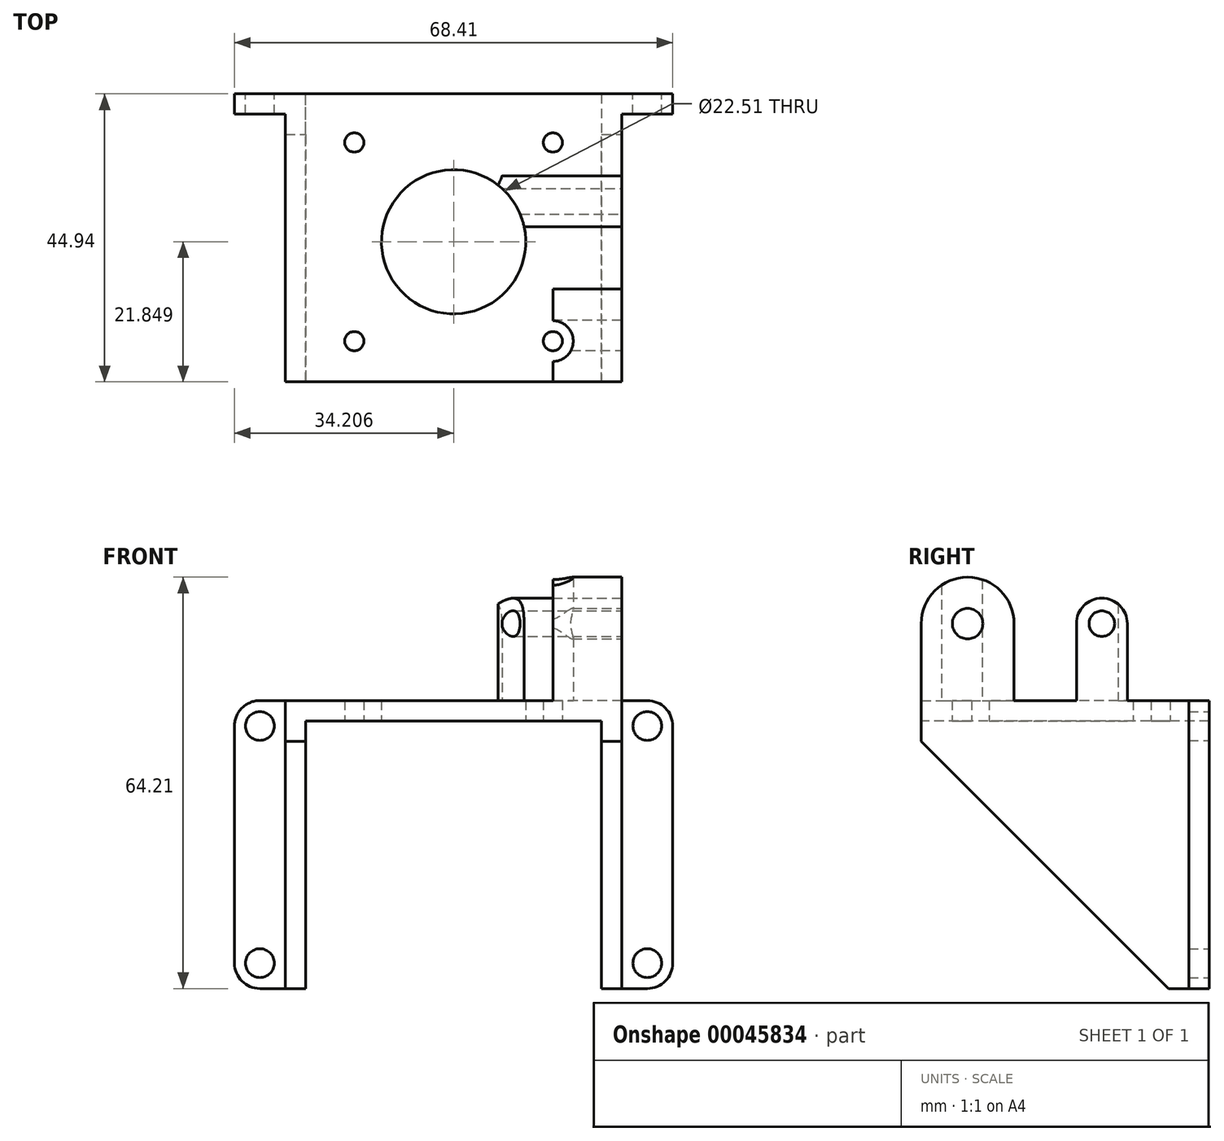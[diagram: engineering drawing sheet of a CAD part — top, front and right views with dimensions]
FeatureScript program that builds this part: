
annotation { "Feature Type Name" : "Feature", "Feature Type Description" : "" }
export const myFeature = defineFeature(function(context is Context, id is Id, definition is map)
    precondition{}
    {
        {
            var Q0;
            Q0=qCreatedBy(makeId("Top.planeOp"),FACE);
            var sketch = newSketch(context, id + "F0", { "sketchPlane" : qUnion([Q0])});
            skLineSegment(sketch, "E0.bottom", {"start": v(0, 0) * mm, "end": v(52.53, 0) * mm});
            skLineSegment(sketch, "E0.top", {"start": v(0, -44.94) * mm, "end": v(52.53, -44.94) * mm});
            skLineSegment(sketch, "E0.left", {"start": v(0, 0) * mm, "end": v(0, -44.94) * mm});
            skLineSegment(sketch, "E0.right", {"start": v(52.53, 0) * mm, "end": v(52.53, -44.94) * mm});
            skLineSegment(sketch, "E1.rect.bottom", {"start": v(41.77, -7.6) * mm, "end": v(10.77, -7.6) * mm, "construction": true});
            skLineSegment(sketch, "E1.rect.top", {"start": v(41.77, -38.6) * mm, "end": v(10.77, -38.6) * mm, "construction": true});
            skLineSegment(sketch, "E1.rect.left", {"start": v(41.77, -7.6) * mm, "end": v(41.77, -38.6) * mm, "construction": true});
            skLineSegment(sketch, "E1.rect.right", {"start": v(10.77, -7.6) * mm, "end": v(10.77, -38.6) * mm, "construction": true});
            skPoint(sketch, "E1.rect.middle", {"position": v(26.27, -23.1) * mm});
            skCircle(sketch, "E2", {"center": v(10.77, -7.6) * mm, "radius": 1.5 * mm});
            skCircle(sketch, "E3", {"center": v(26.27, -23.1) * mm, "radius": 11.25 * mm});
            skCircle(sketch, "E4", {"center": v(41.77, -7.6) * mm, "radius": 1.5 * mm});
            skCircle(sketch, "E5", {"center": v(41.77, -38.6) * mm, "radius": 1.5 * mm});
            skCircle(sketch, "E6", {"center": v(10.77, -38.6) * mm, "radius": 1.5 * mm});
            skLineSegment(sketch, "E7", {"start": v(26.27, -23.1) * mm, "end": v(26.27, 0) * mm, "construction": true});
            skCircle(sketch, "E8", {"center": v(10.77, -38.6) * mm, "radius": 6.35 * mm, "construction": true});
            skSolve(sketch);
        }
        {
            var Q0;
            Q0=qSketchRegion(id+"F0",true);
            extrude(context, id + "F1", {"entities" : qUnion([Q0]), "depth" : 3.17 * mm});
        }
        {
            var Q0;
            Q0=makeQuery(id+"F1.opExtrude","CAP_FACE",FACE,{"disambiguationData":[OSD([sQuery(id+"F0.wireOp",EDGE,"E0.bottom"),sQuery(id+"F0.wireOp",EDGE,"E0.top"),sQuery(id+"F0.wireOp",EDGE,"E0.left"),sQuery(id+"F0.wireOp",EDGE,"E0.right"),sQuery(id+"F0.wireOp",EDGE,"E2"),sQuery(id+"F0.wireOp",EDGE,"E3"),sQuery(id+"F0.wireOp",EDGE,"E4"),sQuery(id+"F0.wireOp",EDGE,"E5"),sQuery(id+"F0.wireOp",EDGE,"E6")])],"isStart":true});
            var sketch = newSketch(context, id + "F2", { "sketchPlane" : qUnion([Q0])});
            skLineSegment(sketch, "E9.bottom", {"start": v(0, 44.94) * mm, "end": v(3.18, 44.94) * mm});
            skLineSegment(sketch, "E9.top", {"start": v(0, 0) * mm, "end": v(3.18, 0) * mm});
            skLineSegment(sketch, "E9.left", {"start": v(0, 44.94) * mm, "end": v(0, 0) * mm});
            skLineSegment(sketch, "E9.right", {"start": v(3.18, 44.94) * mm, "end": v(3.18, 0) * mm});
            skLineSegment(sketch, "E10.bottom", {"start": v(52.53, 0) * mm, "end": v(49.36, 0) * mm});
            skLineSegment(sketch, "E10.top", {"start": v(52.53, 44.94) * mm, "end": v(49.36, 44.94) * mm});
            skLineSegment(sketch, "E10.left", {"start": v(52.53, 0) * mm, "end": v(52.53, 44.94) * mm});
            skLineSegment(sketch, "E10.right", {"start": v(49.36, 0) * mm, "end": v(49.36, 44.94) * mm});
            skSolve(sketch);
        }
        {
            var Q0;
            Q0=qSketchRegion(id+"F2",true);
            extrude(context, id + "F3", {"entities" : qUnion([Q0]), "operationType" : NewBodyOperationType.ADD, "depth" : 41.77 * mm});
        }
        {
            var Q0;
            Q0=makeQuery(id+"F3.opExtrude","CAP_FACE",FACE,{"disambiguationData":[OSD([sQuery(id+"F2.wireOp",EDGE,"E9.bottom"),sQuery(id+"F2.wireOp",EDGE,"E9.top"),sQuery(id+"F2.wireOp",EDGE,"E9.left"),sQuery(id+"F2.wireOp",EDGE,"E9.right")])],"isStart":false});
            var sketch = newSketch(context, id + "F4", { "sketchPlane" : qUnion([Q0])});
            skLineSegment(sketch, "E11.bottom", {"start": v(0, 0) * mm, "end": v(-7.94, 0) * mm});
            skLineSegment(sketch, "E11.top", {"start": v(0, 3.18) * mm, "end": v(-7.94, 3.18) * mm});
            skLineSegment(sketch, "E11.left", {"start": v(0, 0) * mm, "end": v(0, 3.18) * mm});
            skLineSegment(sketch, "E11.right", {"start": v(-7.94, 0) * mm, "end": v(-7.94, 3.18) * mm});
            skLineSegment(sketch, "E12.bottom", {"start": v(52.53, 0) * mm, "end": v(60.47, 0) * mm});
            skLineSegment(sketch, "E12.top", {"start": v(52.53, 3.18) * mm, "end": v(60.47, 3.18) * mm});
            skLineSegment(sketch, "E12.left", {"start": v(52.53, 0) * mm, "end": v(52.53, 3.18) * mm});
            skLineSegment(sketch, "E12.right", {"start": v(60.47, 0) * mm, "end": v(60.47, 3.18) * mm});
            skSolve(sketch);
        }
        {
            var Q0;
            Q0=qSketchRegion(id+"F4",true);
            var Q1;
            Q1=makeQuery(id+"F1.opExtrude","CAP_FACE",FACE,{"disambiguationData":[OSD([sQuery(id+"F0.wireOp",EDGE,"E0.bottom"),sQuery(id+"F0.wireOp",EDGE,"E0.top"),sQuery(id+"F0.wireOp",EDGE,"E0.left"),sQuery(id+"F0.wireOp",EDGE,"E0.right"),sQuery(id+"F0.wireOp",EDGE,"E2"),sQuery(id+"F0.wireOp",EDGE,"E3"),sQuery(id+"F0.wireOp",EDGE,"E4"),sQuery(id+"F0.wireOp",EDGE,"E5"),sQuery(id+"F0.wireOp",EDGE,"E6")])],"isStart":false});
            extrude(context, id + "F5", {"entities" : qUnion([Q0]), "operationType" : NewBodyOperationType.ADD, "endBound" : BoundingType.UP_TO_SURFACE, "oppositeDirection" : true, "endBoundEntityFace" : qUnion([Q1]), "depth" : 25.4 * mm});
        }
        {
            var Q0;
            Q0=makeQuery(id+"F5.opExtrude","CAP_EDGE",EDGE,{"disambiguationData":[OSD([sQuery(id+"F4.wireOp",EDGE,"E12.right")])],"isStart":true});
            var Q1;
            Q1=makeQuery(id+"F5.opExtrude","CAP_EDGE",EDGE,{"disambiguationData":[OSD([sQuery(id+"F4.wireOp",EDGE,"E12.right")])],"isStart":false});
            var Q2;
            Q2=makeQuery(id+"F5.opExtrude","CAP_EDGE",EDGE,{"disambiguationData":[OSD([sQuery(id+"F4.wireOp",EDGE,"E11.right")])],"isStart":false});
            var Q3;
            Q3=makeQuery(id+"F5.opExtrude","CAP_EDGE",EDGE,{"disambiguationData":[OSD([sQuery(id+"F4.wireOp",EDGE,"E11.right")])],"isStart":true});
            fillet(context, id + "F6", {"entities" : qUnion([Q0, Q1, Q2, Q3]), "radius" : 3.97 * mm, "tangentPropagation" : true, "allowEdgeOverflow" : false});
        }
        {
            var Q0;
            Q0=makeQuery(id+"F5.boolean.opBoolean","MERGE",FACE,{"derivedFrom":[makeQuery(id+"F3.boolean.opBoolean","MERGE",FACE,{"derivedFrom":[makeQuery(id+"F1.opExtrude","SWEPT_FACE",FACE,{"disambiguationData":[OSD([sQuery(id+"F0.wireOp",EDGE,"E0.bottom")])]}),makeQuery(id+"F3.opExtrude","SWEPT_FACE",FACE,{"disambiguationData":[OSD([sQuery(id+"F2.wireOp",EDGE,"E9.top")])]}),makeQuery(id+"F3.opExtrude","SWEPT_FACE",FACE,{"disambiguationData":[OSD([sQuery(id+"F2.wireOp",EDGE,"E10.bottom")])]})]}),makeQuery(id+"F5.opExtrude","SWEPT_FACE",FACE,{"disambiguationData":[OSD([sQuery(id+"F4.wireOp",EDGE,"E11.bottom")])]}),makeQuery(id+"F5.opExtrude","SWEPT_FACE",FACE,{"disambiguationData":[OSD([sQuery(id+"F4.wireOp",EDGE,"E12.bottom")])]})]});
            var sketch = newSketch(context, id + "F7", { "sketchPlane" : qUnion([Q0])});
            skCircle(sketch, "E13", {"center": v(3.97, -37.8) * mm, "radius": 2.25 * mm});
            skCircle(sketch, "E14", {"center": v(3.97, -0.8) * mm, "radius": 2.25 * mm});
            skCircle(sketch, "E15", {"center": v(-56.5, -0.8) * mm, "radius": 2.25 * mm});
            skCircle(sketch, "E16", {"center": v(-56.5, -37.8) * mm, "radius": 2.25 * mm});
            skSolve(sketch);
        }
        {
            var Q0;
            Q0=qSketchRegion(id+"F7",true);
            var Q1;
            Q1=makeQuery(id+"F5.opExtrude","SWEPT_FACE",FACE,{"disambiguationData":[OSD([sQuery(id+"F4.wireOp",EDGE,"E12.top")])]});
            extrude(context, id + "F8", {"entities" : qUnion([Q0]), "operationType" : NewBodyOperationType.REMOVE, "endBound" : BoundingType.UP_TO_SURFACE, "oppositeDirection" : true, "endBoundEntityFace" : qUnion([Q1]), "depth" : 25.4 * mm});
        }
        {
            var Q0;
            Q0=makeQuery(id+"F3.boolean.opBoolean","MERGE",FACE,{"derivedFrom":[makeQuery(id+"F1.opExtrude","SWEPT_FACE",FACE,{"disambiguationData":[OSD([sQuery(id+"F0.wireOp",EDGE,"E0.right")])]}),makeQuery(id+"F3.opExtrude","SWEPT_FACE",FACE,{"disambiguationData":[OSD([sQuery(id+"F2.wireOp",EDGE,"E10.left")])]})]});
            var sketch = newSketch(context, id + "F9", { "sketchPlane" : qUnion([Q0])});
            skLineSegment(sketch, "E17.top", {"start": v(-44.94, -41.77) * mm, "end": v(-6.35, -41.77) * mm});
            skLineSegment(sketch, "E17.left", {"start": v(-44.94, -3.18) * mm, "end": v(-44.94, -41.77) * mm});
            skLineSegment(sketch, "E18", {"start": v(-44.94, -3.18) * mm, "end": v(-44.94, 0) * mm, "construction": true});
            skLineSegment(sketch, "E19", {"start": v(-6.35, -41.77) * mm, "end": v(-3.18, -41.77) * mm, "construction": true});
            skLineSegment(sketch, "E20", {"start": v(-6.35, -41.77) * mm, "end": v(-44.94, -3.17) * mm});
            skSolve(sketch);
        }
        {
            var Q0;
            Q0=qSketchRegion(id+"F9",true);
            var Q1;
            Q1=makeQuery(id+"F3.boolean.opBoolean","MERGE",FACE,{"derivedFrom":[makeQuery(id+"F1.opExtrude","SWEPT_FACE",FACE,{"disambiguationData":[OSD([sQuery(id+"F0.wireOp",EDGE,"E0.left")])]}),makeQuery(id+"F3.opExtrude","SWEPT_FACE",FACE,{"disambiguationData":[OSD([sQuery(id+"F2.wireOp",EDGE,"E9.left")])]})]});
            extrude(context, id + "F10", {"entities" : qUnion([Q0]), "operationType" : NewBodyOperationType.REMOVE, "endBound" : BoundingType.UP_TO_SURFACE, "oppositeDirection" : true, "endBoundEntityFace" : qUnion([Q1]), "depth" : 25.4 * mm});
        }
        {
            var Q0;
            Q0=makeQuery(id+"F5.boolean.opBoolean","MERGE",FACE,{"derivedFrom":[makeQuery(id+"F1.opExtrude","CAP_FACE",FACE,{"disambiguationData":[OSD([sQuery(id+"F0.wireOp",EDGE,"E0.bottom"),sQuery(id+"F0.wireOp",EDGE,"E0.top"),sQuery(id+"F0.wireOp",EDGE,"E0.left"),sQuery(id+"F0.wireOp",EDGE,"E0.right"),sQuery(id+"F0.wireOp",EDGE,"E2"),sQuery(id+"F0.wireOp",EDGE,"E3"),sQuery(id+"F0.wireOp",EDGE,"E4"),sQuery(id+"F0.wireOp",EDGE,"E5"),sQuery(id+"F0.wireOp",EDGE,"E6")])],"isStart":false}),makeQuery(id+"F5.opExtrude","CAP_FACE",FACE,{"disambiguationData":[OSD([sQuery(id+"F4.wireOp",EDGE,"E11.bottom"),sQuery(id+"F4.wireOp",EDGE,"E11.top"),sQuery(id+"F4.wireOp",EDGE,"E11.left"),sQuery(id+"F4.wireOp",EDGE,"E11.right")])],"isStart":false}),makeQuery(id+"F5.opExtrude","CAP_FACE",FACE,{"disambiguationData":[OSD([sQuery(id+"F4.wireOp",EDGE,"E12.bottom"),sQuery(id+"F4.wireOp",EDGE,"E12.top"),sQuery(id+"F4.wireOp",EDGE,"E12.left"),sQuery(id+"F4.wireOp",EDGE,"E12.right")])],"isStart":false})]});
            var sketch = newSketch(context, id + "F11", { "sketchPlane" : qUnion([Q0])});
            skLineSegment(sketch, "E21.bottom", {"start": v(52.53, -44.94) * mm, "end": v(41.77, -44.94) * mm});
            skLineSegment(sketch, "E21.top", {"start": v(52.53, -30.44) * mm, "end": v(41.77, -30.44) * mm});
            skLineSegment(sketch, "E21.left", {"start": v(52.53, -44.94) * mm, "end": v(52.53, -30.44) * mm});
            skArc(sketch, "E22", {"start": v(41.77, -41.77) * mm, "mid": v(44.94, -38.6) * mm, "end": v(41.77, -35.42) * mm});
            skLineSegment(sketch, "E23", {"start": v(41.77, -44.94) * mm, "end": v(41.77, -41.77) * mm});
            skLineSegment(sketch, "E24", {"start": v(41.77, -41.77) * mm, "end": v(41.77, -35.42) * mm, "construction": true});
            skLineSegment(sketch, "E25", {"start": v(41.77, -35.42) * mm, "end": v(41.77, -30.44) * mm});
            skLineSegment(sketch, "E26", {"start": v(26.27, -23.1) * mm, "end": v(26.27, -16.74) * mm, "construction": true});
            skLineSegment(sketch, "E27.top", {"start": v(52.53, -12.77) * mm, "end": v(30.75, -12.77) * mm});
            skLineSegment(sketch, "E27.left", {"start": v(52.53, -20.7) * mm, "end": v(52.53, -12.77) * mm});
            skLineSegment(sketch, "E27.right", {"start": v(30.75, -20.7) * mm, "end": v(30.75, -12.77) * mm});
            skLineSegment(sketch, "E28", {"start": v(26.27, -16.74) * mm, "end": v(30.75, -16.74) * mm, "construction": true});
            skLineSegment(sketch, "E29", {"start": v(52.53, -20.7) * mm, "end": v(37.26, -20.7) * mm});
            skLineSegment(sketch, "E30", {"start": v(37.26, -20.7) * mm, "end": v(30.75, -20.7) * mm, "construction": true});
            skArc(sketch, "E31", {"start": v(37.26, -20.7) * mm, "mid": v(34.97, -15.96) * mm, "end": v(30.75, -12.77) * mm});
            skSolve(sketch);
        }
        {
            var Q0;
            Q0=qSketchRegion(id+"F11",true);
            var Q1;
            {var subQ2=sQuery(id+"F11.wireOp",EDGE,"330cf8d8-da5a-4c49-9072-953a09258db2.bottom");Q1=makeQuery(id+"F11.imprint","IMPRINT",FACE,{"disambiguationData":[TD([[makeQuery(id+"F11.imprint","IMPRINT",EDGE,{"derivedFrom":subQ2}),1.0]])]});}
            extrude(context, id + "F12", {"entities" : qUnion([Q0, Q1]), "operationType" : NewBodyOperationType.ADD, "depth" : 19.27 * mm});
        }
        {
            var Q0;
            Q0=makeQuery(id+"F12.boolean.opBoolean","MERGE",FACE,{"derivedFrom":[makeQuery(id+"F3.boolean.opBoolean","MERGE",FACE,{"derivedFrom":[makeQuery(id+"F1.opExtrude","SWEPT_FACE",FACE,{"disambiguationData":[OSD([sQuery(id+"F0.wireOp",EDGE,"E0.right")])]}),makeQuery(id+"F3.opExtrude","SWEPT_FACE",FACE,{"disambiguationData":[OSD([sQuery(id+"F2.wireOp",EDGE,"E10.left")])]})]}),makeQuery(id+"F12.opExtrude","SWEPT_FACE",FACE,{"disambiguationData":[OSD([sQuery(id+"F11.wireOp",EDGE,"E21.left")])]})]});
            var sketch = newSketch(context, id + "F13", { "sketchPlane" : qUnion([Q0])});
            skLineSegment(sketch, "E32", {"start": v(-37.69, 15.19) * mm, "end": v(-37.69, 3.17) * mm});
            skLineSegment(sketch, "E33", {"start": v(-30.44, 3.18) * mm, "end": v(-37.69, 3.17) * mm});
            skLineSegment(sketch, "E34", {"start": v(-37.69, 15.19) * mm, "end": v(-44.94, 15.19) * mm});
            skCircle(sketch, "E35", {"center": v(-37.69, 15.19) * mm, "radius": 2.38 * mm});
            skSolve(sketch);
        }
        {
            var Q0;
            Q0=qSketchRegion(id+"F13",true);
            var Q1;
            Q1=makeQuery(id+"F12.opExtrude","SWEPT_FACE",FACE,{"disambiguationData":[OSD([sQuery(id+"F11.wireOp",EDGE,"E25")])]});
            extrude(context, id + "F14", {"entities" : qUnion([Q0]), "operationType" : NewBodyOperationType.REMOVE, "endBound" : BoundingType.UP_TO_SURFACE, "oppositeDirection" : true, "endBoundEntityFace" : qUnion([Q1]), "depth" : 25.4 * mm});
        }
        {
            var Q0;
            Q0=makeQuery(id+"F12.opExtrude","CAP_EDGE",EDGE,{"disambiguationData":[OSD([sQuery(id+"F11.wireOp",EDGE,"E21.bottom")])],"isStart":false});
            var Q1;
            Q1=makeQuery(id+"F12.opExtrude","CAP_EDGE",EDGE,{"disambiguationData":[OSD([sQuery(id+"F11.wireOp",EDGE,"E21.top")])],"isStart":false});
            fillet(context, id + "F15", {"entities" : qUnion([Q0, Q1]), "radius" : 7.25 * mm, "tangentPropagation" : true, "allowEdgeOverflow" : false});
        }
        {
            var Q0;
            Q0=makeQuery(id+"F12.boolean.opBoolean","MERGE",FACE,{"derivedFrom":[makeQuery(id+"F3.boolean.opBoolean","MERGE",FACE,{"derivedFrom":[makeQuery(id+"F1.opExtrude","SWEPT_FACE",FACE,{"disambiguationData":[OSD([sQuery(id+"F0.wireOp",EDGE,"E0.right")])]}),makeQuery(id+"F3.opExtrude","SWEPT_FACE",FACE,{"disambiguationData":[OSD([sQuery(id+"F2.wireOp",EDGE,"E10.left")])]})]}),makeQuery(id+"F12.opExtrude","SWEPT_FACE",FACE,{"disambiguationData":[OSD([sQuery(id+"F11.wireOp",EDGE,"E21.left")])]}),makeQuery(id+"F12.opExtrude","SWEPT_FACE",FACE,{"disambiguationData":[OSD([sQuery(id+"F11.wireOp",EDGE,"E27.left")])]})]});
            var sketch = newSketch(context, id + "F16", { "sketchPlane" : qUnion([Q0])});
            skLineSegment(sketch, "E36.bottom", {"start": v(-20.7, 22.44) * mm, "end": v(-12.77, 22.44) * mm});
            skLineSegment(sketch, "E36.top", {"start": v(-20.7, 15.19) * mm, "end": v(-12.77, 15.19) * mm, "construction": true});
            skLineSegment(sketch, "E36.left", {"start": v(-20.7, 22.44) * mm, "end": v(-20.7, 15.19) * mm});
            skLineSegment(sketch, "E36.right", {"start": v(-12.77, 22.44) * mm, "end": v(-12.77, 15.19) * mm});
            skLineSegment(sketch, "E37", {"start": v(-37.69, 15.19) * mm, "end": v(-20.7, 15.19) * mm, "construction": true});
            skArc(sketch, "E38", {"start": v(-12.77, 15.19) * mm, "mid": v(-16.74, 19.16) * mm, "end": v(-20.7, 15.19) * mm});
            skCircle(sketch, "E39", {"center": v(-16.74, 15.19) * mm, "radius": 2 * mm});
            skSolve(sketch);
        }
        {
            var Q0;
            Q0=qSketchRegion(id+"F16",true);
            var Q1;
            Q1=makeQuery(id+"F12.boolean.opBoolean","MERGE",FACE,{"derivedFrom":[makeQuery(id+"F1.opExtrude","SWEPT_FACE",FACE,{"disambiguationData":[OSD([sQuery(id+"F0.wireOp",EDGE,"E3")])]}),makeQuery(id+"F12.opExtrude","SWEPT_FACE",FACE,{"disambiguationData":[OSD([sQuery(id+"F11.wireOp",EDGE,"E31")])]})]});
            extrude(context, id + "F17", {"entities" : qUnion([Q0]), "operationType" : NewBodyOperationType.REMOVE, "endBound" : BoundingType.UP_TO_SURFACE, "oppositeDirection" : true, "endBoundEntityFace" : qUnion([Q1]), "depth" : 25.4 * mm});
        }
        {
            var Q0;
            Q0=makeQuery(id+"F5.boolean.opBoolean","MERGE",FACE,{"derivedFrom":[makeQuery(id+"F1.opExtrude","CAP_FACE",FACE,{"disambiguationData":[OSD([sQuery(id+"F0.wireOp",EDGE,"E0.bottom"),sQuery(id+"F0.wireOp",EDGE,"E0.top"),sQuery(id+"F0.wireOp",EDGE,"E0.left"),sQuery(id+"F0.wireOp",EDGE,"E0.right"),sQuery(id+"F0.wireOp",EDGE,"E2"),sQuery(id+"F0.wireOp",EDGE,"E3"),sQuery(id+"F0.wireOp",EDGE,"E4"),sQuery(id+"F0.wireOp",EDGE,"E5"),sQuery(id+"F0.wireOp",EDGE,"E6")])],"isStart":false}),makeQuery(id+"F5.opExtrude","CAP_FACE",FACE,{"disambiguationData":[OSD([sQuery(id+"F4.wireOp",EDGE,"E11.bottom"),sQuery(id+"F4.wireOp",EDGE,"E11.top"),sQuery(id+"F4.wireOp",EDGE,"E11.left"),sQuery(id+"F4.wireOp",EDGE,"E11.right")])],"isStart":false}),makeQuery(id+"F5.opExtrude","CAP_FACE",FACE,{"disambiguationData":[OSD([sQuery(id+"F4.wireOp",EDGE,"E12.bottom"),sQuery(id+"F4.wireOp",EDGE,"E12.top"),sQuery(id+"F4.wireOp",EDGE,"E12.left"),sQuery(id+"F4.wireOp",EDGE,"E12.right")])],"isStart":false})]});
            var sketch = newSketch(context, id + "F18", { "sketchPlane" : qUnion([Q0])});
            skCircle(sketch, "E40", {"center": v(26.27, -23.1) * mm, "radius": 6.35 * mm, "construction": true});
            skCircle(sketch, "E41", {"center": v(26.27, -10.4) * mm, "radius": 6.35 * mm, "construction": true});
            skLineSegment(sketch, "E42", {"start": v(26.27, -23.1) * mm, "end": v(26.27, -10.4) * mm, "construction": true});
            skCircle(sketch, "E43", {"center": v(26.27, -10.4) * mm, "radius": 7.94 * mm});
            skSolve(sketch);
        }
        {
            var Q0;
            Q0=qSketchRegion(id+"F18",true);
            extrude(context, id + "F19", {"entities" : qUnion([Q0]), "operationType" : NewBodyOperationType.REMOVE, "depth" : 25.4 * mm});
        }
    });
